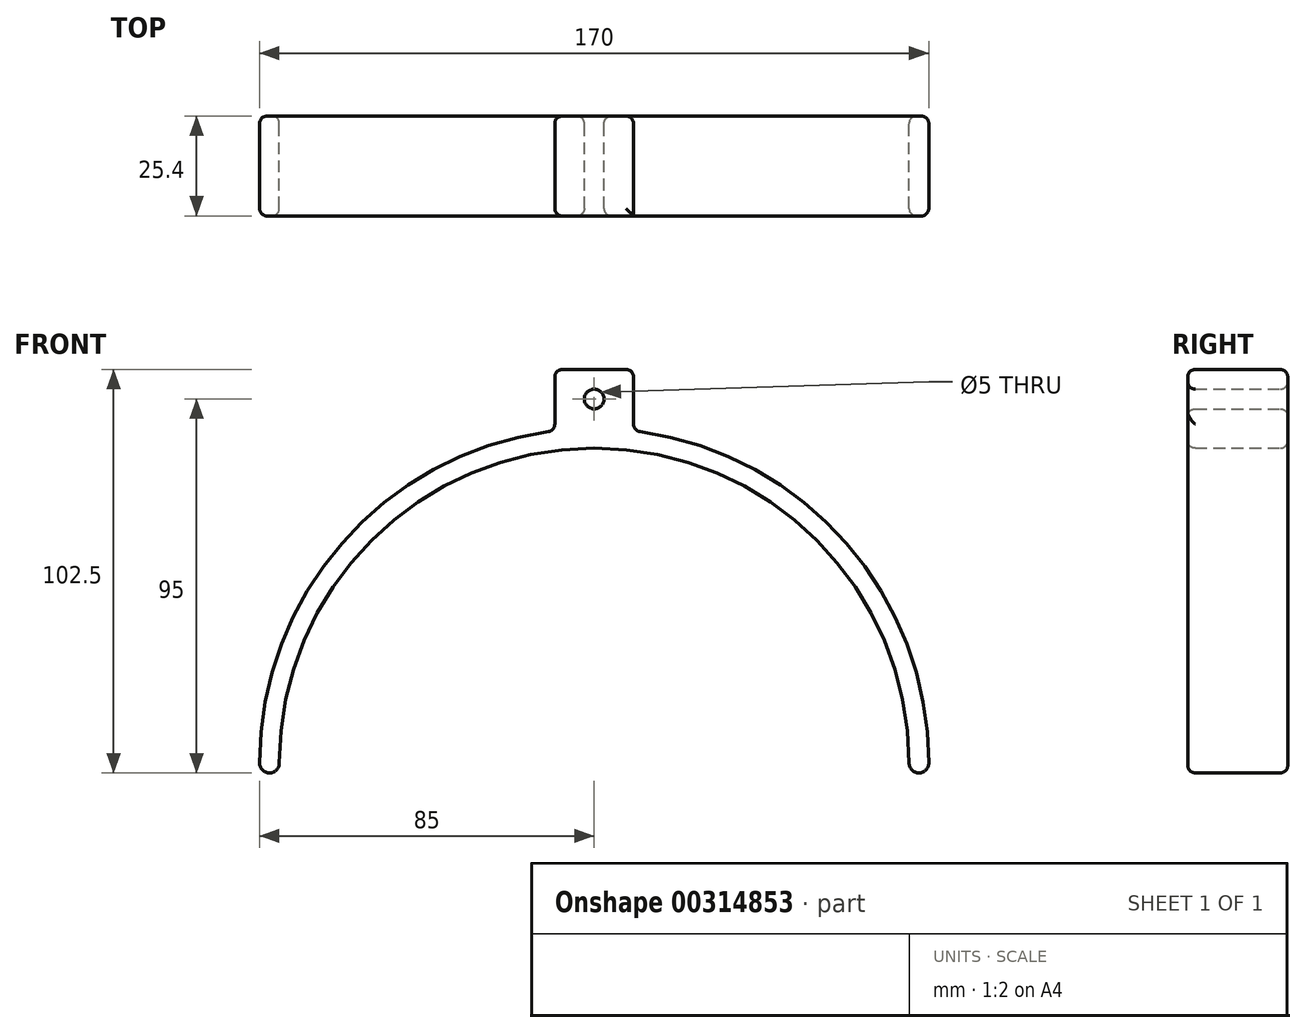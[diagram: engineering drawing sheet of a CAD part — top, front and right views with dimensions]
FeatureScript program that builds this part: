
annotation { "Feature Type Name" : "Feature", "Feature Type Description" : "" }
export const myFeature = defineFeature(function(context is Context, id is Id, definition is map)
    precondition{}
    {
        {
            var Q0;
            Q0=qCreatedBy(makeId("Front.planeOp"),FACE);
            var sketch = newSketch(context, id + "F0", { "sketchPlane" : qUnion([Q0])});
            skArc(sketch, "E0", {"start": v(80, 0) * mm, "mid": v(0, 80) * mm, "end": v(-80, 0) * mm});
            skArc(sketch, "E1", {"start": v(85, 0) * mm, "mid": v(0, 85) * mm, "end": v(-85, 0) * mm});
            skLineSegment(sketch, "E2", {"start": v(0, 80) * mm, "end": v(0, 85) * mm, "construction": true});
            skLineSegment(sketch, "E3.bottom", {"start": v(0, 100) * mm, "end": v(0, 100) * mm});
            skLineSegment(sketch, "E3.top", {"start": v(0, 85) * mm, "end": v(0, 85) * mm});
            skLineSegment(sketch, "E4", {"start": v(0, 100) * mm, "end": v(0, 85) * mm, "construction": true});
            skLineSegment(sketch, "E5.bottom", {"start": v(10, 100) * mm, "end": v(0, 100) * mm, "construction": true});
            skLineSegment(sketch, "E5.left", {"start": v(10, 100) * mm, "end": v(10, 85) * mm, "construction": true});
            skLineSegment(sketch, "E6.top", {"start": v(0, 100) * mm, "end": v(-10, 100) * mm, "construction": true});
            skLineSegment(sketch, "E6.left", {"start": v(0, 85) * mm, "end": v(0, 100) * mm, "construction": true});
            skLineSegment(sketch, "E6.right", {"start": v(-10, 85) * mm, "end": v(-10, 100) * mm, "construction": true});
            skLineSegment(sketch, "E7.bottom", {"start": v(-10, 100) * mm, "end": v(10, 100) * mm});
            skLineSegment(sketch, "E7.left", {"start": v(-10, 100) * mm, "end": v(-10, 79.37) * mm});
            skLineSegment(sketch, "E7.right", {"start": v(10, 100) * mm, "end": v(10, 79.37) * mm});
            skLineSegment(sketch, "E8", {"start": v(-10, 100) * mm, "end": v(10, 85) * mm, "construction": true});
            skLineSegment(sketch, "E9", {"start": v(10, 100) * mm, "end": v(-10, 85) * mm, "construction": true});
            skCircle(sketch, "E10", {"center": v(0, 92.5) * mm, "radius": 2.5 * mm});
            skLineSegment(sketch, "E11", {"start": v(0, 0) * mm, "end": v(-85, 0) * mm, "construction": true});
            skLineSegment(sketch, "E12", {"start": v(0, 0) * mm, "end": v(85, 0) * mm, "construction": true});
            skLineSegment(sketch, "E13", {"start": v(-85, 0) * mm, "end": v(-80, 0) * mm, "construction": true});
            skCircle(sketch, "E14", {"center": v(-82.5, 0) * mm, "radius": 2.5 * mm});
            skLineSegment(sketch, "E15", {"start": v(85, 0) * mm, "end": v(80, 0) * mm, "construction": true});
            skArc(sketch, "E16", {"start": v(80, 0) * mm, "mid": v(82.5, -2.5) * mm, "end": v(85, 0) * mm});
            skSolve(sketch);
        }
        {
            var Q0;
            {var subQ0=sQuery(id+"F0.wireOp",EDGE,"E14");var subQ1=makeQuery(id+"F0.imprint","INTERSECT",VERTEX,{"derivedFrom":[sQuery(id+"F0.wireOp",EDGE,"E0"),subQ0]});Q0=makeQuery(id+"F0.imprint","IMPRINT",FACE,{"disambiguationData":[TD([[makeQuery(id+"F0.imprint","IMPRINT",EDGE,{"disambiguationData":[TD([[subQ1,-1.0]])],"derivedFrom":subQ0}),1.0]])]});}
            var Q1;
            {var subQ0=sQuery(id+"F0.wireOp",EDGE,"E14");var subQ1=sQuery(id+"F0.wireOp",EDGE,"E0");var subQ2=makeQuery(id+"F0.imprint","INTERSECT",VERTEX,{"derivedFrom":[subQ1,subQ0]});Q1=makeQuery(id+"F0.imprint","IMPRINT",FACE,{"disambiguationData":[TD([[makeQuery(id+"F0.imprint","IMPRINT",EDGE,{"disambiguationData":[TD([[subQ2,1.0]])],"derivedFrom":subQ1}),-1.0]])]});}
            var Q2;
            {var subQ1=sQuery(id+"F0.wireOp",EDGE,"E7.bottom");Q2=makeQuery(id+"F0.imprint","IMPRINT",FACE,{"disambiguationData":[TD([[makeQuery(id+"F0.imprint","IMPRINT",EDGE,{"derivedFrom":subQ1}),-1.0]])]});}
            var Q3;
            {var subQ0=sQuery(id+"F0.wireOp",EDGE,"E7.left");var subQ1=sQuery(id+"F0.wireOp",EDGE,"E0");var subQ2=makeQuery(id+"F0.imprint","INTERSECT",VERTEX,{"derivedFrom":[subQ1,subQ0]});Q3=makeQuery(id+"F0.imprint","IMPRINT",FACE,{"disambiguationData":[TD([[makeQuery(id+"F0.imprint","IMPRINT",EDGE,{"disambiguationData":[TD([[subQ2,1.0]])],"derivedFrom":subQ1}),-1.0]])]});}
            var Q4;
            {var subQ0=sQuery(id+"F0.wireOp",EDGE,"E16");Q4=makeQuery(id+"F0.imprint","IMPRINT",FACE,{"disambiguationData":[TD([[makeQuery(id+"F0.imprint","IMPRINT",EDGE,{"derivedFrom":subQ0}),1.0]])]});}
            extrude(context, id + "F1", {"entities" : qUnion([Q0, Q1, Q2, Q3, Q4]), "depth" : 25.4 * mm});
        }
        {
            var Q0;
            {var subQ0=sQuery(id+"F0.wireOp",EDGE,"E1");Q0=makeQuery(id+"F1.opExtrude","SWEPT_FACE",FACE,{"disambiguationData":[OSD([subQ0]),TDD([makeQuery(id+"F0.imprint","IMPRINT",EDGE,{"disambiguationData":[TD([[makeQuery(id+"F0.imprint","INTERSECT",VERTEX,{"derivedFrom":[subQ0,sQuery(id+"F0.wireOp",EDGE,"E16")]}),-1.0]])],"derivedFrom":subQ0})])]});}
            var Q1;
            Q1=makeQuery(id+"F1.opExtrude","CAP_FACE",FACE,{"disambiguationData":[OSD([sQuery(id+"F0.wireOp",EDGE,"E0"),sQuery(id+"F0.wireOp",EDGE,"E1"),sQuery(id+"F0.wireOp",EDGE,"E7.bottom"),sQuery(id+"F0.wireOp",EDGE,"E7.left"),sQuery(id+"F0.wireOp",EDGE,"E7.right"),sQuery(id+"F0.wireOp",EDGE,"E10"),sQuery(id+"F0.wireOp",EDGE,"E14"),sQuery(id+"F0.wireOp",EDGE,"E16")])],"isStart":true});
            var Q2;
            Q2=makeQuery(id+"F1.opExtrude","CAP_EDGE",EDGE,{"disambiguationData":[OSD([sQuery(id+"F0.wireOp",EDGE,"E10")])],"isStart":false});
            var Q3;
            Q3=makeQuery(id+"F1.opExtrude","SWEPT_FACE",FACE,{"disambiguationData":[OSD([sQuery(id+"F0.wireOp",EDGE,"E7.left")])]});
            var Q4;
            Q4=makeQuery(id+"F1.opExtrude","SWEPT_FACE",FACE,{"disambiguationData":[OSD([sQuery(id+"F0.wireOp",EDGE,"E7.bottom")])]});
            fillet(context, id + "F2", {"entities" : qUnion([Q0, Q1, Q2, Q3, Q4]), "radius" : 1.9 * mm, "tangentPropagation" : true, "allowEdgeOverflow" : false});
        }
    });
